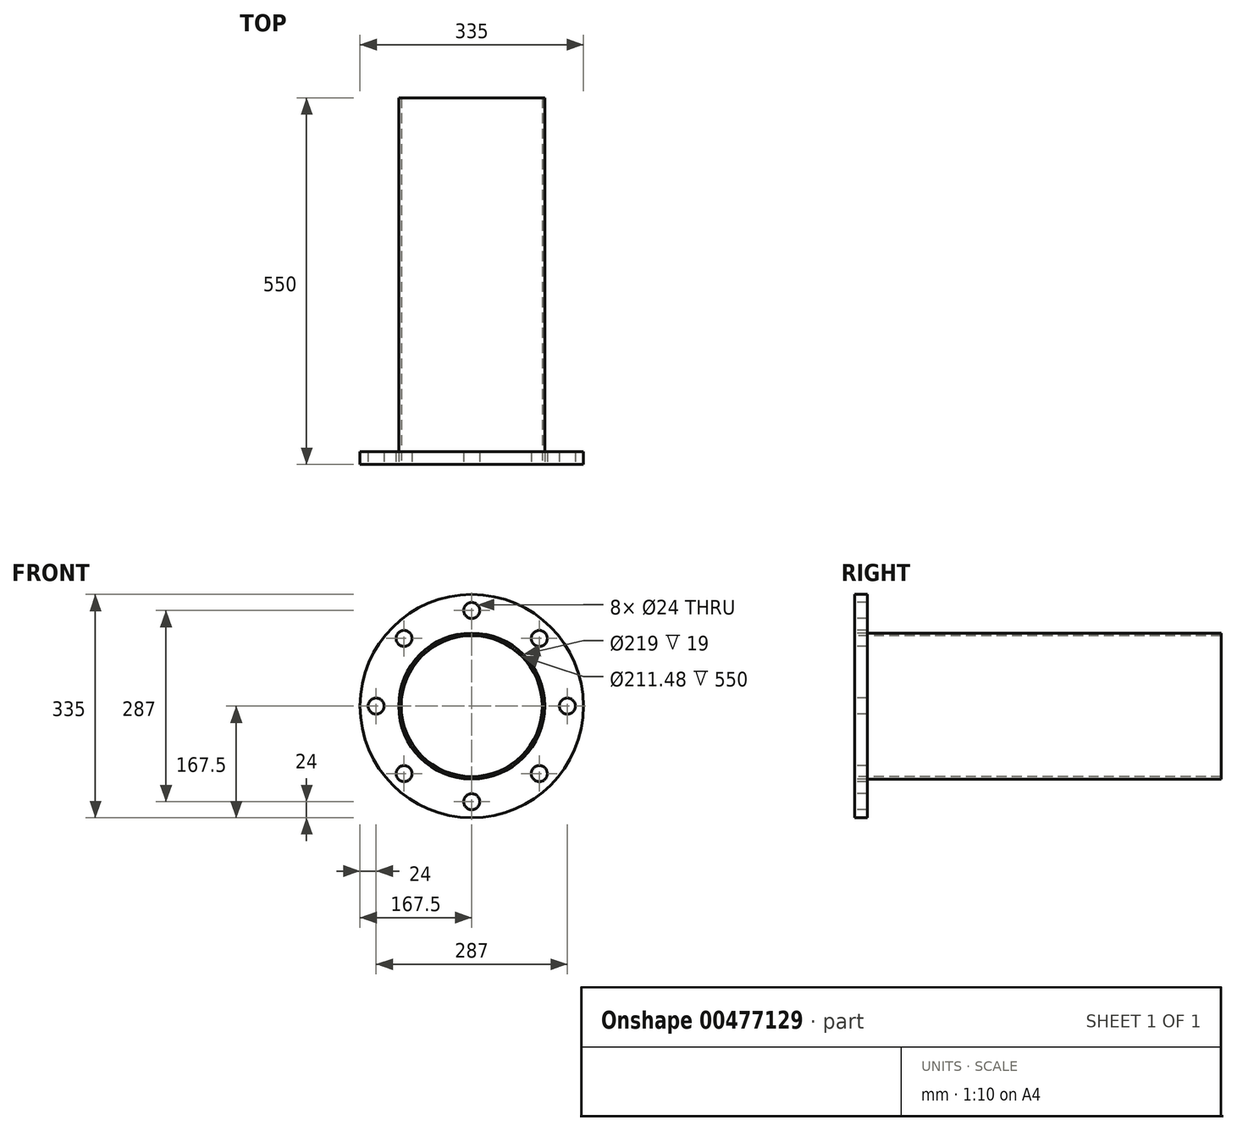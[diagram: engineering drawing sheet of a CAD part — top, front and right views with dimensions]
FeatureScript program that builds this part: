
annotation { "Feature Type Name" : "Feature", "Feature Type Description" : "" }
export const myFeature = defineFeature(function(context is Context, id is Id, definition is map)
    precondition{}
    {
        {
            var Q0;
            Q0=qCreatedBy(makeId("Front.planeOp"),FACE);
            var sketch = newSketch(context, id + "F0", { "sketchPlane" : qUnion([Q0])});
            skCircle(sketch, "E0", {"center": v(0, 0) * mm, "radius": 109.5 * mm});
            skCircle(sketch, "E1", {"center": v(0, 0) * mm, "radius": 105.74 * mm});
            skSolve(sketch);
        }
        {
            assignVariable(context, id + "F1", {"name" : "pipeLength", "anyValue" : 550});
        }
        {
            var Q0;
            Q0=makeQuery(id+"F0.imprint","IMPRINT",FACE,{"disambiguationData":[TD([[makeQuery(id+"F0.imprint","IMPRINT",EDGE,{"derivedFrom":sQuery(id+"F0.wireOp",EDGE,"E0")}),1.0]])]});
            extrude(context, id + "F2", {"entities" : qUnion([Q0]), "oppositeDirection" : true, "depth" : (getVariable(context, 'pipeLength')) * mm, "offsetDistance" : 25 * mm});
        }
        {
            var Q0;
            Q0=qCreatedBy(makeId("Front.planeOp"),FACE);
            var sketch = newSketch(context, id + "F3", { "sketchPlane" : qUnion([Q0])});
            skCircle(sketch, "E2.0", {"center": v(0, 0) * mm, "radius": 109.5 * mm});
            skCircle(sketch, "E3", {"center": v(0, 0) * mm, "radius": 167.5 * mm});
            skLineSegment(sketch, "E4", {"start": v(0, 0) * mm, "end": v(0, 167.5) * mm, "construction": true});
            skCircle(sketch, "E5", {"center": v(0, 143.5) * mm, "radius": 12 * mm});
            skCircle(sketch, "E6.1.0", {"center": v(-101.47, 101.47) * mm, "radius": 12 * mm});
            skCircle(sketch, "E6.2.0", {"center": v(-143.5, 0) * mm, "radius": 12 * mm});
            skCircle(sketch, "E6.3.0", {"center": v(-101.47, -101.47) * mm, "radius": 12 * mm});
            skCircle(sketch, "E6.4.0", {"center": v(0, -143.5) * mm, "radius": 12 * mm});
            skCircle(sketch, "E6.5.0", {"center": v(101.47, -101.47) * mm, "radius": 12 * mm});
            skCircle(sketch, "E6.6.0", {"center": v(143.5, 0) * mm, "radius": 12 * mm});
            skCircle(sketch, "E6.7.0", {"center": v(101.47, 101.47) * mm, "radius": 12 * mm});
            skSolve(sketch);
        }
        {
            var Q0;
            Q0=makeQuery(id+"F3.imprint","IMPRINT",FACE,{"disambiguationData":[TD([[makeQuery(id+"F3.imprint","IMPRINT",EDGE,{"derivedFrom":sQuery(id+"F3.wireOp",EDGE,"E2.0")}),-1.0]])]});
            extrude(context, id + "F4", {"entities" : qUnion([Q0]), "oppositeDirection" : true, "depth" : 19 * mm, "offsetDistance" : 25 * mm});
        }
        {
            var Q0;
            Q0=qCreatedBy(makeId("Top.planeOp"),FACE);
            var sketch = newSketch(context, id + "F5", { "sketchPlane" : qUnion([Q0])});
            skLineSegment(sketch, "E7", {"start": v(-109.5, 0) * mm, "end": v(-109.5, 500) * mm, "construction": true});
            skLineSegment(sketch, "E8", {"start": v(109.5, 500) * mm, "end": v(109.5, 0) * mm, "construction": true});
            skLineSegment(sketch, "E9.0", {"start": v(167.5, 19) * mm, "end": v(-167.5, 19) * mm, "construction": true});
            skLineSegment(sketch, "E10", {"start": v(-109.5, 69) * mm, "end": v(109.5, 69) * mm, "construction": true});
            skSolve(sketch);
        }
    });
